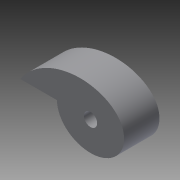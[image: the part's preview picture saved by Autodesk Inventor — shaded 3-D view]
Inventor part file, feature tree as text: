
AUTODESK INVENTOR PART (.ipt)
format: ipt  version: 2014 (Build 180170000, 170)  size: 97,280 bytes
history: native  units: in
note: dims shown in document units (in); Inventor stores cm internally (conversion verified against a paired STEP export)
features: extrude x1, sketch x1
ambient origin geometry x8: Origin, YZ Plane, XZ Plane, XY Plane, X Axis, Y Axis, Z Axis, Center Point
bodies: Solid1 (feature_tree)
feature tree (2):
  extrude  "Extrusion1"  Depth=0.95in
  sketch  "Sketch1"  dims[d42=1.252in d43=1.9803in d44=0.949in d45=1.2135in d46=0.4555in d47=1.5659in d48=0.8021in d53=0.8623in d57=0.2344in d62=0.95in d63=0.8215in d64=0.375in d65=1.0in d66=0.0in]
